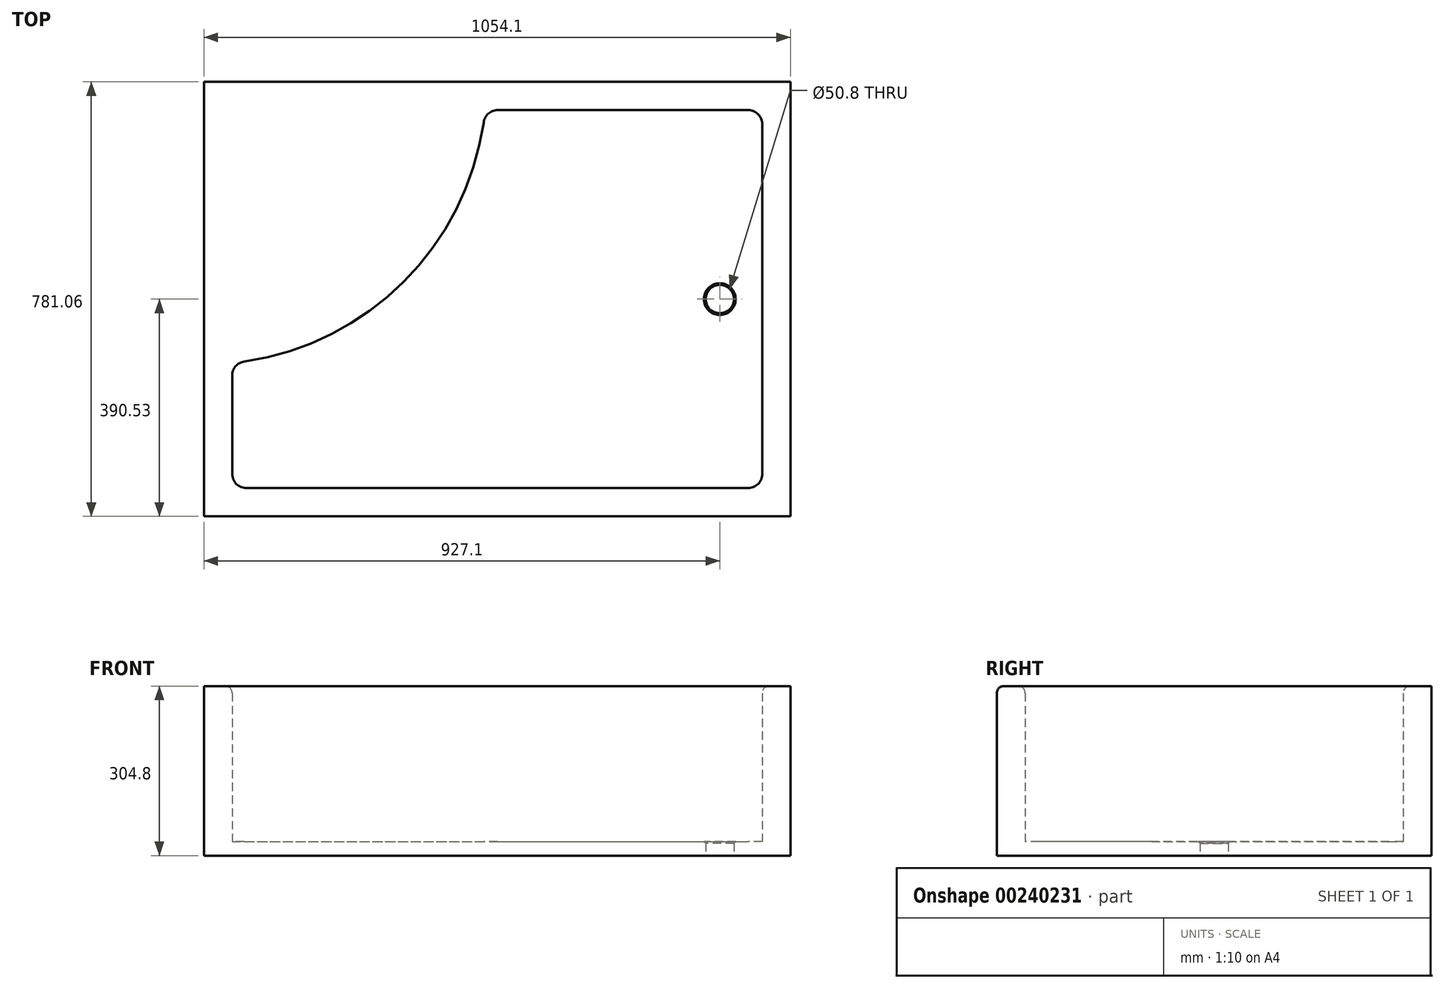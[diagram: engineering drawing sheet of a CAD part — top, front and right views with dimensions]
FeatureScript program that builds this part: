
annotation { "Feature Type Name" : "Feature", "Feature Type Description" : "" }
export const myFeature = defineFeature(function(context is Context, id is Id, definition is map)
    precondition{}
    {
        {
            var Q0;
            Q0=qCreatedBy(makeId("Top.planeOp"),FACE);
            var sketch = newSketch(context, id + "F0", { "sketchPlane" : qUnion([Q0])});
            skLineSegment(sketch, "E0.bottom", {"start": v(527.05, -390.52) * mm, "end": v(-527.05, -390.52) * mm});
            skLineSegment(sketch, "E0.top", {"start": v(527.05, 390.53) * mm, "end": v(-527.05, 390.53) * mm});
            skLineSegment(sketch, "E0.left", {"start": v(527.05, -390.52) * mm, "end": v(527.05, 390.53) * mm});
            skLineSegment(sketch, "E0.right", {"start": v(-527.05, -390.52) * mm, "end": v(-527.05, 390.53) * mm});
            skPoint(sketch, "E0.middle", {"position": v(0, 0) * mm});
            skLineSegment(sketch, "E1.bottom", {"start": v(0.88, 339.73) * mm, "end": v(450.85, 339.73) * mm});
            skLineSegment(sketch, "E1.top", {"start": v(-450.85, -339.73) * mm, "end": v(450.85, -339.73) * mm});
            skLineSegment(sketch, "E1.left", {"start": v(-476.25, -137.4) * mm, "end": v(-476.25, -314.33) * mm});
            skLineSegment(sketch, "E1.right", {"start": v(476.25, 314.33) * mm, "end": v(476.25, -314.33) * mm});
            skArc(sketch, "E2", {"start": v(-454.48, -112.26) * mm, "mid": v(-167.84, 31.31) * mm, "end": v(-24.26, 317.95) * mm});
            skPoint(sketch, "E3.visualSharp", {"position": v(476.25, 339.73) * mm});
            skArc(sketch, "E3.filletArc", {"start": v(476.25, 314.33) * mm, "mid": v(468.81, 332.29) * mm, "end": v(450.85, 339.73) * mm});
            skPoint(sketch, "E4.visualSharp", {"position": v(476.25, -339.73) * mm});
            skArc(sketch, "E4.filletArc", {"start": v(450.85, -339.73) * mm, "mid": v(468.81, -332.29) * mm, "end": v(476.25, -314.33) * mm});
            skPoint(sketch, "E5.visualSharp", {"position": v(-476.25, -339.73) * mm});
            skArc(sketch, "E5.filletArc", {"start": v(-476.25, -314.33) * mm, "mid": v(-468.81, -332.29) * mm, "end": v(-450.85, -339.73) * mm});
            skPoint(sketch, "E6.visualSharp", {"position": v(-476.25, -114.93) * mm});
            skArc(sketch, "E6.filletArc", {"start": v(-454.48, -112.26) * mm, "mid": v(-470.05, -120.78) * mm, "end": v(-476.25, -137.4) * mm});
            skPoint(sketch, "E7.visualSharp", {"position": v(-21.6, 339.73) * mm});
            skArc(sketch, "E7.filletArc", {"start": v(0.88, 339.73) * mm, "mid": v(-15.75, 333.53) * mm, "end": v(-24.26, 317.95) * mm});
            skPoint(sketch, "E8.visualSharp", {"position": v(-527.05, -390.52) * mm});
            skLineSegment(sketch, "E8.filletArc", {"start": v(-527.05, -390.52) * mm, "end": v(-527.05, -390.52) * mm});
            skPoint(sketch, "E9.visualSharp", {"position": v(527.05, -390.52) * mm});
            skLineSegment(sketch, "E9.filletArc", {"start": v(527.05, -390.52) * mm, "end": v(527.05, -390.52) * mm});
            skCircle(sketch, "E10", {"center": v(400.05, 0) * mm, "radius": 25.4 * mm});
            skSolve(sketch);
        }
        {
            var Q0;
            Q0=makeQuery(id+"F0.imprint","IMPRINT",FACE,{"disambiguationData":[TD([[makeQuery(id+"F0.imprint","IMPRINT",EDGE,{"derivedFrom":sQuery(id+"F0.wireOp",EDGE,"E0.bottom")}),-1.0]])]});
            extrude(context, id + "F1", {"entities" : qUnion([Q0]), "depth" : 304.8 * mm});
        }
        {
            var Q0;
            Q0=makeQuery(id+"F0.imprint","IMPRINT",FACE,{"disambiguationData":[TD([[makeQuery(id+"F0.imprint","IMPRINT",EDGE,{"derivedFrom":sQuery(id+"F0.wireOp",EDGE,"E1.bottom")}),-1.0]])]});
            extrude(context, id + "F2", {"entities" : qUnion([Q0]), "operationType" : NewBodyOperationType.ADD, "depth" : 25.4 * mm});
        }
        {
            var Q0;
            Q0=makeQuery(id+"F1.opExtrude","CAP_EDGE",EDGE,{"disambiguationData":[OSD([sQuery(id+"F0.wireOp",EDGE,"E2")])],"isStart":false});
            fillet(context, id + "F3", {"entities" : qUnion([Q0]), "radius" : 12.7 * mm, "tangentPropagation" : true, "allowEdgeOverflow" : false});
        }
        {
            var Q0;
            Q0=makeQuery(id+"F2.opExtrude","CAP_EDGE",EDGE,{"disambiguationData":[OSD([sQuery(id+"F0.wireOp",EDGE,"E10")])],"isStart":false});
            chamfer(context, id + "F4", {"entities" : qUnion([Q0]), "width" : 3.17 * mm, "tangentPropagation" : true});
        }
        {
            var Q0;
            Q0=makeQuery(id+"F1.opExtrude","CAP_EDGE",EDGE,{"disambiguationData":[OSD([sQuery(id+"F0.wireOp",EDGE,"E0.bottom")])],"isStart":false});
            fillet(context, id + "F5", {"entities" : qUnion([Q0]), "radius" : 12.7 * mm, "tangentPropagation" : true, "allowEdgeOverflow" : false});
        }
    });
